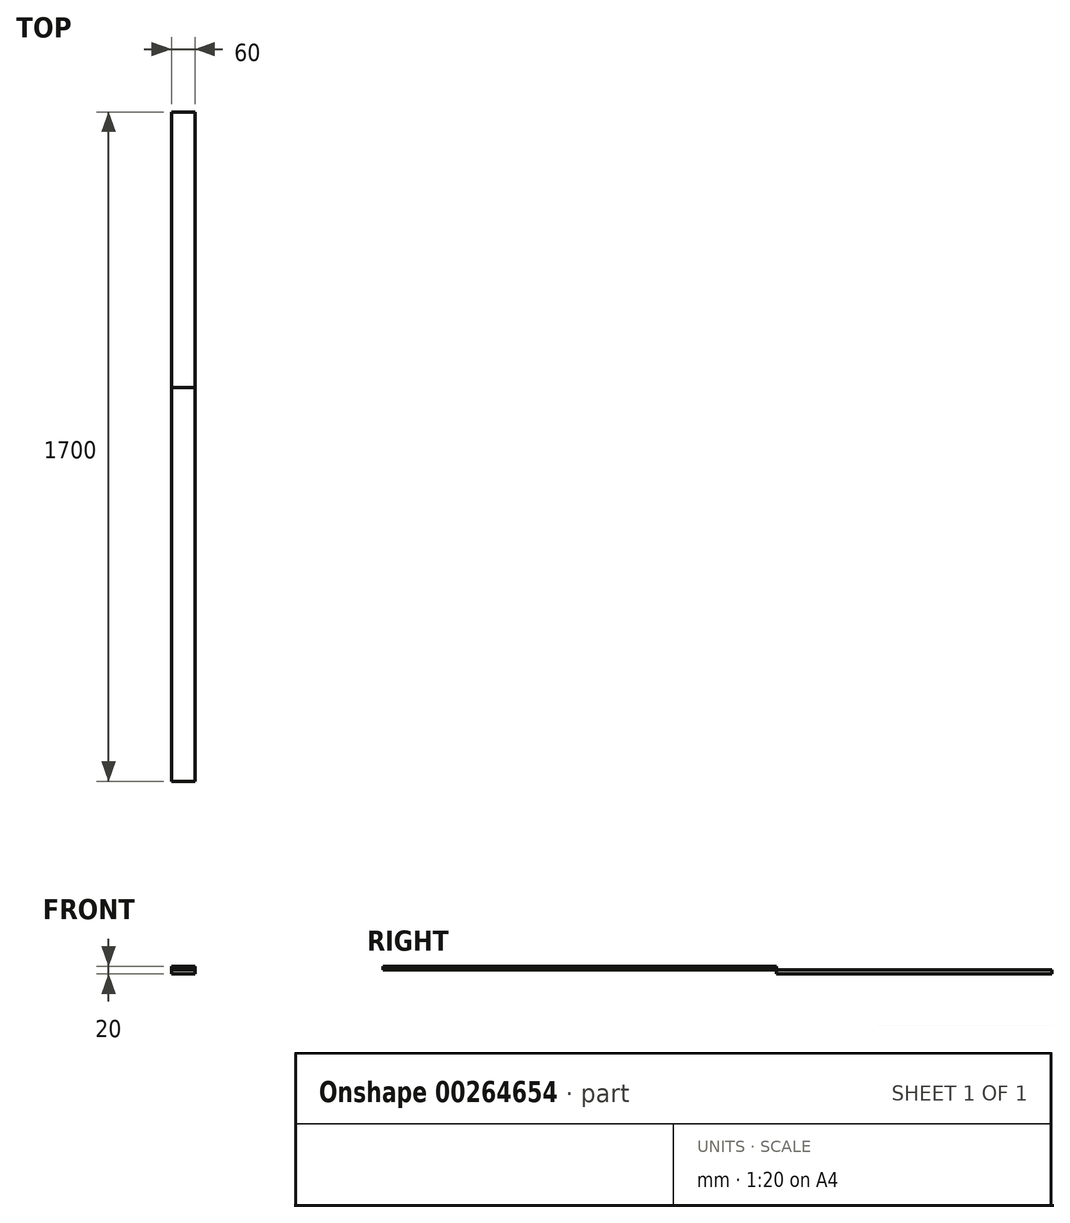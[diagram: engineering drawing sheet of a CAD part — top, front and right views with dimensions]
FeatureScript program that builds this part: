
annotation { "Feature Type Name" : "Feature", "Feature Type Description" : "" }
export const myFeature = defineFeature(function(context is Context, id is Id, definition is map)
    precondition{}
    {
        {
            var Q0;
            Q0=qCreatedBy(makeId("Right.planeOp"),FACE);
            var sketch = newSketch(context, id + "F0", { "sketchPlane" : qUnion([Q0])});
            skLineSegment(sketch, "E0", {"start": v(0, 0) * mm, "end": v(0, 10) * mm});
            skLineSegment(sketch, "E1", {"start": v(0, 10) * mm, "end": v(-1000, 10) * mm});
            skLineSegment(sketch, "E2", {"start": v(-1000, 10) * mm, "end": v(-1000, 0) * mm});
            skLineSegment(sketch, "E3", {"start": v(-1000, 0) * mm, "end": v(700, 0) * mm});
            skLineSegment(sketch, "E4", {"start": v(700, 0) * mm, "end": v(700, -10) * mm});
            skLineSegment(sketch, "E5", {"start": v(700, -10) * mm, "end": v(0, -10) * mm});
            skLineSegment(sketch, "E6", {"start": v(0, -10) * mm, "end": v(0, 0) * mm});
            skSolve(sketch);
        }
        {
            var Q0;
            Q0 = qSketchRegion(id + "F0", true);
            extrude(context, id + "F1", {"entities" : qUnion([Q0]), "endBound" : BoundingType.SYMMETRIC, "depth" : 60 * mm});
        }
    });
